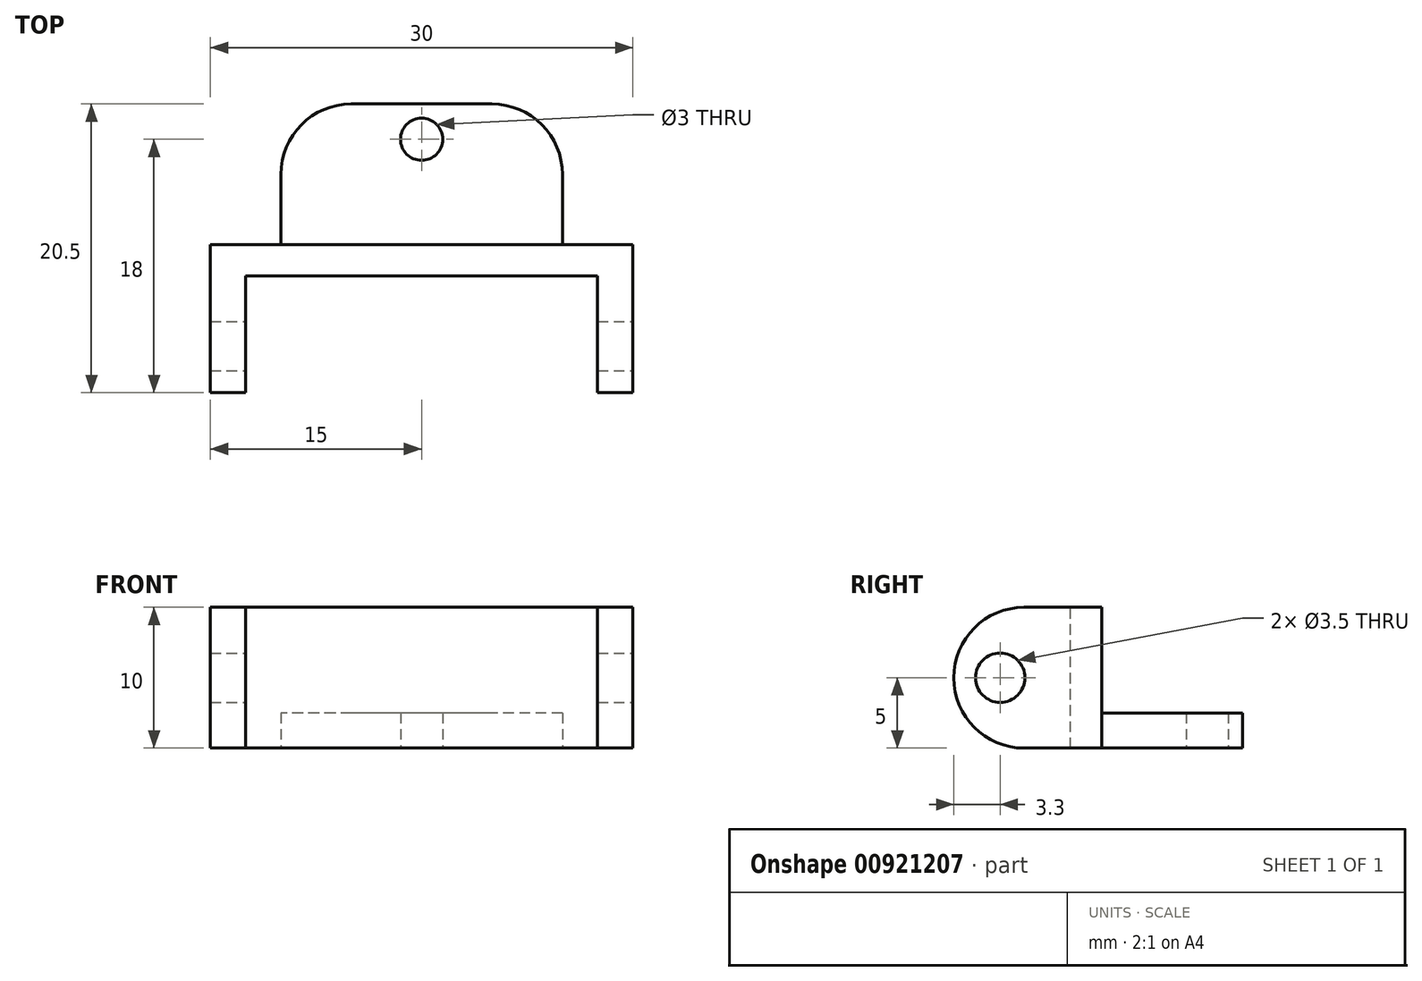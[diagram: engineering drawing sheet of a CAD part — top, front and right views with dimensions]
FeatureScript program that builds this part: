
annotation { "Feature Type Name" : "Feature", "Feature Type Description" : "" }
export const myFeature = defineFeature(function(context is Context, id is Id, definition is map)
    precondition{}
    {
        {
            var Q0;
            Q0=qCreatedBy(makeId("Front.planeOp"),FACE);
            var sketch = newSketch(context, id + "F0", { "sketchPlane" : qUnion([Q0])});
            skLineSegment(sketch, "E0.bottom", {"start": v(12.5, -5) * mm, "end": v(-12.5, -5) * mm});
            skLineSegment(sketch, "E0.top", {"start": v(12.5, 5) * mm, "end": v(-12.5, 5) * mm});
            skLineSegment(sketch, "E0.left", {"start": v(12.5, -5) * mm, "end": v(12.5, 5) * mm});
            skLineSegment(sketch, "E0.right", {"start": v(-12.5, -5) * mm, "end": v(-12.5, 5) * mm});
            skPoint(sketch, "E0.middle", {"position": v(0, 0) * mm});
            skLineSegment(sketch, "E1.bottom", {"start": v(15, -5) * mm, "end": v(-15, -5) * mm});
            skLineSegment(sketch, "E1.top", {"start": v(15, 5) * mm, "end": v(-15, 5) * mm});
            skLineSegment(sketch, "E1.left", {"start": v(15, -5) * mm, "end": v(15, 5) * mm});
            skLineSegment(sketch, "E1.right", {"start": v(-15, -5) * mm, "end": v(-15, 5) * mm});
            skSolve(sketch);
        }
        {
            var Q0;
            {var subQ0=sQuery(id+"F0.wireOp",EDGE,"E0.left");Q0=makeQuery(id+"F0.imprint","IMPRINT",FACE,{"disambiguationData":[TD([[makeQuery(id+"F0.imprint","IMPRINT",EDGE,{"derivedFrom":subQ0}),1.0]])]});}
            extrude(context, id + "F1", {"entities" : qUnion([Q0]), "depth" : 2.2 * mm, "offsetDistance" : 25 * mm});
        }
        {
            var Q0;
            {var subQ0=sQuery(id+"F0.wireOp",EDGE,"E0.right");Q0=makeQuery(id+"F0.imprint","IMPRINT",FACE,{"disambiguationData":[TD([[makeQuery(id+"F0.imprint","IMPRINT",EDGE,{"derivedFrom":subQ0}),1.0]])]});}
            var Q1;
            {var subQ0=sQuery(id+"F0.wireOp",EDGE,"E0.left");Q1=makeQuery(id+"F0.imprint","IMPRINT",FACE,{"disambiguationData":[TD([[makeQuery(id+"F0.imprint","IMPRINT",EDGE,{"derivedFrom":subQ0}),-1.0]])]});}
            extrude(context, id + "F2", {"entities" : qUnion([Q0, Q1]), "operationType" : NewBodyOperationType.ADD, "depth" : 10.5 * mm, "offsetDistance" : 25 * mm});
        }
        {
            var Q0;
            {var subQ0=sQuery(id+"F0.wireOp",EDGE,"E1.top");Q0=makeQuery(id+"F2.opExtrude","CAP_EDGE",EDGE,{"disambiguationData":[OSD([subQ0]),TDD([makeQuery(id+"F0.imprint","IMPRINT",EDGE,{"disambiguationData":[TD([[makeQuery(id+"F0.imprint","INTERSECT",VERTEX,{"derivedFrom":[sQuery(id+"F0.wireOp",EDGE,"E0.left"),subQ0]}),1.0]])],"derivedFrom":subQ0})])],"isStart":false});}
            var Q1;
            {var subQ0=sQuery(id+"F0.wireOp",EDGE,"E1.bottom");Q1=makeQuery(id+"F2.opExtrude","CAP_EDGE",EDGE,{"disambiguationData":[OSD([subQ0]),TDD([makeQuery(id+"F0.imprint","IMPRINT",EDGE,{"disambiguationData":[TD([[makeQuery(id+"F0.imprint","INTERSECT",VERTEX,{"derivedFrom":[sQuery(id+"F0.wireOp",EDGE,"E0.left"),subQ0]}),1.0]])],"derivedFrom":subQ0})])],"isStart":false});}
            var Q2;
            {var subQ0=sQuery(id+"F0.wireOp",EDGE,"E1.bottom");Q2=makeQuery(id+"F2.opExtrude","CAP_EDGE",EDGE,{"disambiguationData":[OSD([subQ0]),TDD([makeQuery(id+"F0.imprint","IMPRINT",EDGE,{"disambiguationData":[TD([[makeQuery(id+"F0.imprint","INTERSECT",VERTEX,{"derivedFrom":[sQuery(id+"F0.wireOp",EDGE,"E0.right"),subQ0]}),-1.0]])],"derivedFrom":subQ0})])],"isStart":false});}
            var Q3;
            {var subQ0=sQuery(id+"F0.wireOp",EDGE,"E1.top");Q3=makeQuery(id+"F2.opExtrude","CAP_EDGE",EDGE,{"disambiguationData":[OSD([subQ0]),TDD([makeQuery(id+"F0.imprint","IMPRINT",EDGE,{"disambiguationData":[TD([[makeQuery(id+"F0.imprint","INTERSECT",VERTEX,{"derivedFrom":[sQuery(id+"F0.wireOp",EDGE,"E0.right"),subQ0]}),-1.0]])],"derivedFrom":subQ0})])],"isStart":false});}
            fillet(context, id + "F3", {"entities" : qUnion([Q0, Q1, Q2, Q3]), "radius" : 5 * mm, "tangentPropagation" : true, "allowEdgeOverflow" : false});
        }
        {
            var Q0;
            Q0=makeQuery(id+"F2.opExtrude","SWEPT_FACE",FACE,{"disambiguationData":[OSD([sQuery(id+"F0.wireOp",EDGE,"E1.left")])]});
            var sketch = newSketch(context, id + "F4", { "sketchPlane" : qUnion([Q0])});
            skCircle(sketch, "E2", {"center": v(-7.2, 0) * mm, "radius": 1.75 * mm});
            skSolve(sketch);
        }
        {
            var Q0;
            Q0=makeQuery(id+"F4.imprint","IMPRINT",FACE,{"disambiguationData":[TD([[makeQuery(id+"F4.imprint","IMPRINT",EDGE,{"derivedFrom":sQuery(id+"F4.wireOp",EDGE,"E2")}),1.0]])]});
            extrude(context, id + "F5", {"entities" : qUnion([Q0]), "operationType" : NewBodyOperationType.REMOVE, "oppositeDirection" : true, "depth" : 35 * mm, "offsetDistance" : 25 * mm});
        }
        {
            var Q0;
            {var subQ0=sQuery(id+"F0.wireOp",EDGE,"E1.top");var subQ1=sQuery(id+"F0.wireOp",EDGE,"E1.bottom");var subQ2=sQuery(id+"F0.wireOp",EDGE,"E0.right");var subQ3=sQuery(id+"F0.wireOp",EDGE,"E0.left");Q0=makeQuery(id+"F2.boolean.opBoolean","MERGE",FACE,{"derivedFrom":[makeQuery(id+"F1.opExtrude","CAP_FACE",FACE,{"disambiguationData":[OSD([subQ3,subQ2,subQ1,subQ0])],"isStart":true}),makeQuery(id+"F2.opExtrude","CAP_FACE",FACE,{"disambiguationData":[OSD([subQ3,subQ1,subQ0,sQuery(id+"F0.wireOp",EDGE,"E1.left")])],"isStart":true}),makeQuery(id+"F2.opExtrude","CAP_FACE",FACE,{"disambiguationData":[OSD([subQ2,subQ1,subQ0,sQuery(id+"F0.wireOp",EDGE,"E1.right")])],"isStart":true})]});}
            var sketch = newSketch(context, id + "F6", { "sketchPlane" : qUnion([Q0])});
            skLineSegment(sketch, "E3.bottom", {"start": v(-10, -2.5) * mm, "end": v(10, -2.5) * mm});
            skLineSegment(sketch, "E3.top", {"start": v(-10, -5) * mm, "end": v(10, -5) * mm});
            skLineSegment(sketch, "E3.left", {"start": v(-10, -2.5) * mm, "end": v(-10, -5) * mm});
            skLineSegment(sketch, "E3.right", {"start": v(10, -2.5) * mm, "end": v(10, -5) * mm});
            skPoint(sketch, "E3.middle", {"position": v(0, -3.75) * mm});
            skSolve(sketch);
        }
        {
            var Q0;
            Q0=makeQuery(id+"F6.imprint","IMPRINT",FACE,{"disambiguationData":[TD([[makeQuery(id+"F6.imprint","IMPRINT",EDGE,{"derivedFrom":sQuery(id+"F6.wireOp",EDGE,"E3.bottom")}),-1.0]])]});
            extrude(context, id + "F7", {"entities" : qUnion([Q0]), "operationType" : NewBodyOperationType.ADD, "depth" : 10 * mm, "offsetDistance" : 25 * mm});
        }
        {
            var Q0;
            Q0=makeQuery(id+"F7.opExtrude","CAP_EDGE",EDGE,{"disambiguationData":[OSD([sQuery(id+"F6.wireOp",EDGE,"E3.left")])],"isStart":false});
            var Q1;
            Q1=makeQuery(id+"F7.opExtrude","CAP_EDGE",EDGE,{"disambiguationData":[OSD([sQuery(id+"F6.wireOp",EDGE,"E3.right")])],"isStart":false});
            fillet(context, id + "F8", {"entities" : qUnion([Q0, Q1]), "radius" : 5 * mm, "tangentPropagation" : true, "allowEdgeOverflow" : false});
        }
        {
            var Q0;
            {var subQ0=sQuery(id+"F0.wireOp",EDGE,"E1.bottom");Q0=makeQuery(id+"F7.boolean.opBoolean","MERGE",FACE,{"derivedFrom":[makeQuery(id+"F2.boolean.opBoolean","MERGE",FACE,{"derivedFrom":[makeQuery(id+"F1.opExtrude","SWEPT_FACE",FACE,{"disambiguationData":[OSD([subQ0])]}),makeQuery(id+"F2.opExtrude","SWEPT_FACE",FACE,{"disambiguationData":[OSD([subQ0]),TDD([makeQuery(id+"F0.imprint","IMPRINT",EDGE,{"disambiguationData":[TD([[makeQuery(id+"F0.imprint","INTERSECT",VERTEX,{"derivedFrom":[sQuery(id+"F0.wireOp",EDGE,"E0.left"),subQ0]}),1.0]])],"derivedFrom":subQ0})])]}),makeQuery(id+"F2.opExtrude","SWEPT_FACE",FACE,{"disambiguationData":[OSD([subQ0]),TDD([makeQuery(id+"F0.imprint","IMPRINT",EDGE,{"disambiguationData":[TD([[makeQuery(id+"F0.imprint","INTERSECT",VERTEX,{"derivedFrom":[sQuery(id+"F0.wireOp",EDGE,"E0.right"),subQ0]}),-1.0]])],"derivedFrom":subQ0})])]})]}),makeQuery(id+"F7.opExtrude","SWEPT_FACE",FACE,{"disambiguationData":[OSD([sQuery(id+"F6.wireOp",EDGE,"E3.top")])]})]});}
            var sketch = newSketch(context, id + "F9", { "sketchPlane" : qUnion([Q0])});
            skCircle(sketch, "E4", {"center": v(0, -7.5) * mm, "radius": 1.5 * mm});
            skSolve(sketch);
        }
        {
            var Q0;
            Q0=makeQuery(id+"F9.imprint","IMPRINT",FACE,{"disambiguationData":[TD([[makeQuery(id+"F9.imprint","IMPRINT",EDGE,{"derivedFrom":sQuery(id+"F9.wireOp",EDGE,"E4")}),1.0]])]});
            extrude(context, id + "F10", {"entities" : qUnion([Q0]), "operationType" : NewBodyOperationType.REMOVE, "oppositeDirection" : true, "depth" : 25 * mm, "offsetDistance" : 25 * mm});
        }
    });
